# Revit family: Bottle_Filler-Murdock-H2O-To-Go-BF16S
name_source: partatom
category: Plumbing Fixtures
units: mm (PartAtom-declared; Revit-internal decimal feet)

## family parameters
Cut with Voids When Loaded = Yes
Host = Face
OmniClass Number = 23.65.70.14.11
OmniClass Title = Drinking Fountains/Coolers
Part Type = Normal
Room Calculation Point = No
Round Connector Dimension = Use Diameter
Shared = Yes

## types (3) — shared parameters
-AP Auto-Purge Function Controller1 = No
-EG22 Enviro-Glaze® Matte Black Powder Coat = No
-WF1 1500-Gallon Capacity Water Filter1 = No
-WF3000 3000-Gallon PFAS Water Filter1 = No
A9100080-A 8 GPH Remote Water Chiller = No
ADA Compliant = Yes
Assembly Code = D2010820
CW Connection = Yes
CWFU = 1.5
Cold Water Connection Diameter = 3/8"
Cold Water Connection Height = 19 3/8"
Cold Water Connection Radius = 3/16"
Cold Water Connection Width = 2"
Default Elevation = 0"
Description = Wall-Mounted, SpringH2O® Touchless All-Stainless Steel Water Bottle Filling Station - Non-Refrigerated, ADA, Standalone
Flow Rate = 1.2 GPM (4.54 l/min) at 70 PSI
HW Connection = No
HWFU = 1.5
Height = 29"
Housing Material = Stainless Steel-Murdock-Satin
IAPMO Compliance = IAPMO tested to NSF/ANSI 61, Section 9, Lead-Free Federal Law 111-380
Installation Type = Wall Mounted
Length = 17 3/4"
Manufacturer = Murdock Mfg.
Material = Stainless Steel-Murdock-Satin
Product Documentation Link = https://www.murdockmfg.com
Product Page URL = https://www.murdockmfg.com
URL = https://www.murdockmfg.com
Vent Connection = No
WFU = 2
Waste Connection = No
Width = 6 5/8"

## per-type parameters (varying)
| type | -BCD Bottle Counter / Filter Status Display | Type Comments |
| BF16S | No | Sensor Operated Stainless Steel Bottle Filler |
| BF16S-BCD | Yes | Sensor Operated Stainless Steel Wall Mount Bottle Filler with Bottle Counter / Filter Status Display |
| BF16S-BAT | No | Battery Sensor Operated Stainless Steel Wall Mount Bottle Filler (N/A with -BCD Bottle Counter Display) |

note: column(s) folded — value = type name in every type: Model

## geometry (parser evidence)
native form markers: Sweep x3
no freeform markers — native parametric forms only
